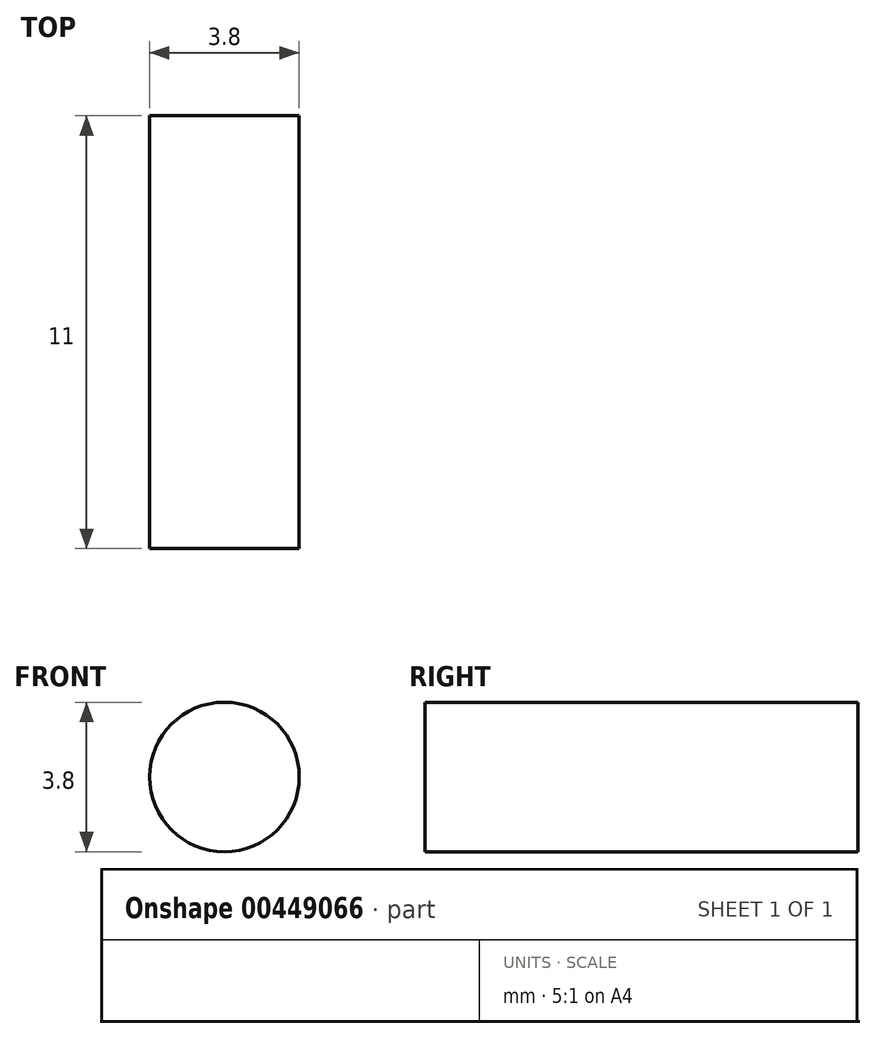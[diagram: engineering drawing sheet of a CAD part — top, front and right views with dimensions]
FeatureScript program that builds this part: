
annotation { "Feature Type Name" : "Feature", "Feature Type Description" : "" }
export const myFeature = defineFeature(function(context is Context, id is Id, definition is map)
    precondition{}
    {
        {
            var Q0;
            Q0=qCreatedBy(makeId("Front.planeOp"),FACE);
            var sketch = newSketch(context, id + "F0", { "sketchPlane" : qUnion([Q0])});
            skCircle(sketch, "E0", {"center": v(0, 0) * mm, "radius": 1.9 * mm});
            skSolve(sketch);
        }
        {
            var Q0;
            Q0=makeQuery(id+"F0.imprint","IMPRINT",FACE,{"disambiguationData":[TD([[makeQuery(id+"F0.imprint","IMPRINT",EDGE,{"derivedFrom":sQuery(id+"F0.wireOp",EDGE,"E0")}),1.0]])]});
            extrude(context, id + "F1", {"entities" : qUnion([Q0]), "depth" : (2 * 5 + 1 * 1) * mm});
        }
    });
